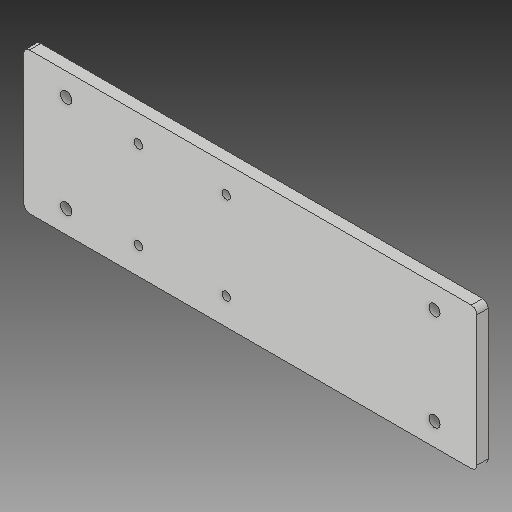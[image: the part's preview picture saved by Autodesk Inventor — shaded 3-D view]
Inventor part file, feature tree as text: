
AUTODESK INVENTOR PART (.ipt)
format: ipt  version: 2019 (Build 230136000, 136)  size: 126,464 bytes
history: native  units: in
note: dims shown in document units (in); Inventor stores cm internally (conversion verified against a paired STEP export)
features: reference x7, other x4, extrude x2, sketch x2, fillet x1, helix x1
ambient origin geometry x8: Origin, YZ Plane, XZ Plane, XY Plane, X Axis, Y Axis, Z Axis, Center Point
bodies: Solid1 (feature_tree)
feature tree (17):
  extrude  "Extrusion1"  Depth=0.1575in TaperAngle=0.0deg
  fillet  "Fillet1"  Radius=0.0787in
  extrude  "Extrusion2"  Depth=0.1575in
  sketch  "Sketch1"  dims[d0=1.9685in d1=0.1575in d2=0.0in d3=0.0787in]
  reference  "Reference1"
  sketch  "Sketch2"  dims[d4=0.1575in d5=0.1575in d6=0.1181in d7=0.1181in d8=0.1181in d9=0.1181in d10=0.1575in d11=0.1575in d12=0.315in d13=0.315in d14=0.315in d15=0.315in d16=0.1575in d17=0.0in]
  reference  "Reference2"
  reference  "Reference3"
  reference  "Reference4"
  reference  "Reference5"
  reference  "Reference6"
  reference  "Reference7"
  other  "<userpath>\Documents\CAD Files\Helix DLP\Helix DLP.iam"
  helix  "Helix DLP.iam"  [1 undecoded]
  other  "30X30 - T-slot - Aluminium Profile:3"
  other  "30X30 - T-slot - Aluminium Profile:1"
  other  "M1173041- NEMA 17 Screw rod:2"
note: 1 required parameter value undecoded (feature->parameter linkage not recoverable at this tier; creation-order binding heuristic only, values carry confidence <= 0.55)
